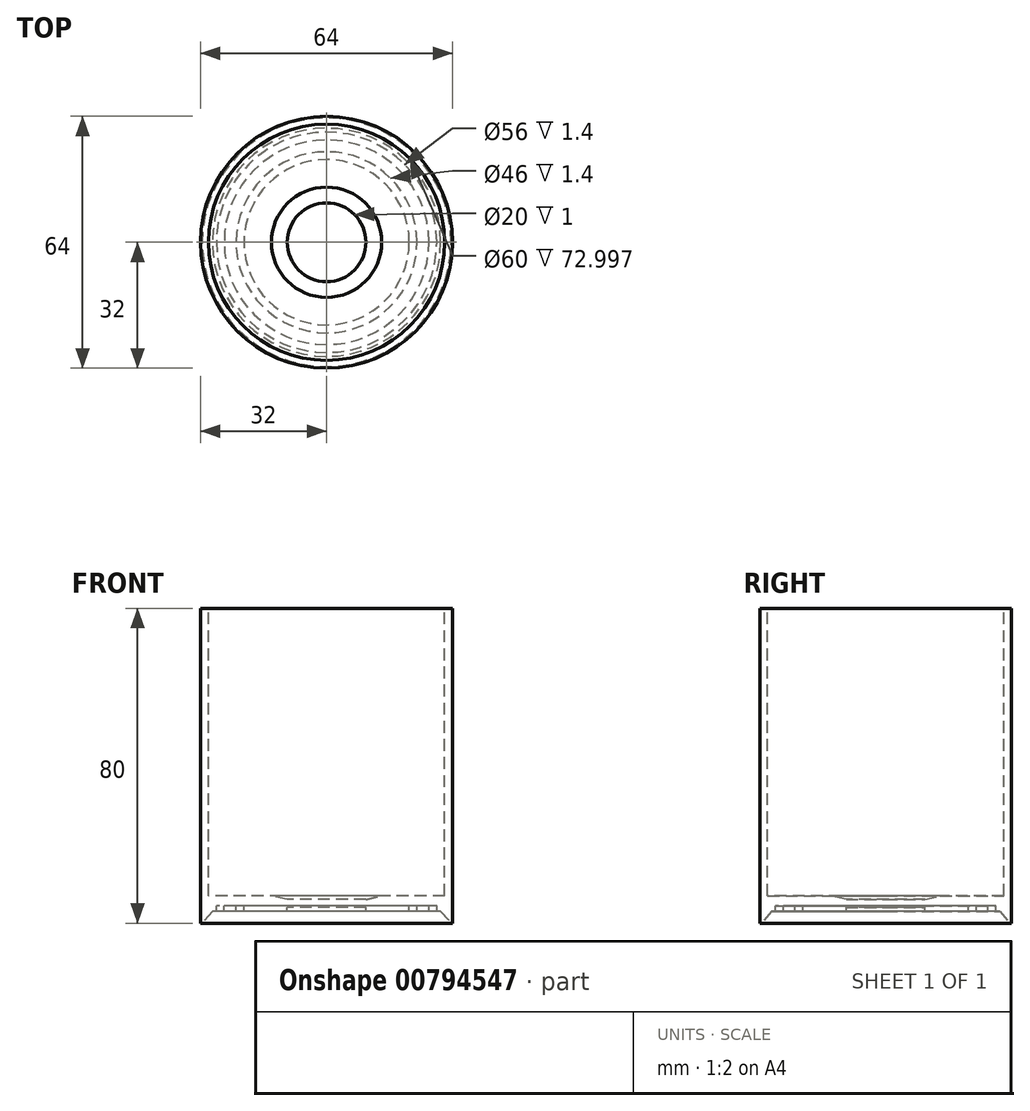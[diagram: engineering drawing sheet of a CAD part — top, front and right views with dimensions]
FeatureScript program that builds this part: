
annotation { "Feature Type Name" : "Feature", "Feature Type Description" : "" }
export const myFeature = defineFeature(function(context is Context, id is Id, definition is map)
    precondition{}
    {
        {
            var Q0;
            Q0=qCreatedBy(makeId("Front.planeOp"),FACE);
            var sketch = newSketch(context, id + "F0", { "sketchPlane" : qUnion([Q0])});
            skLineSegment(sketch, "E0", {"start": v(0, 4) * mm, "end": v(-10, 4) * mm});
            skLineSegment(sketch, "E1", {"start": v(-31.6, 0) * mm, "end": v(-32, 0) * mm});
            skLineSegment(sketch, "E2", {"start": v(-32, 0) * mm, "end": v(-32, 80) * mm});
            skLineSegment(sketch, "E3", {"start": v(-32, 80) * mm, "end": v(-30, 80) * mm});
            skLineSegment(sketch, "E4", {"start": v(-30, 80) * mm, "end": v(-30, 7) * mm});
            skLineSegment(sketch, "E5", {"start": v(-10, 6) * mm, "end": v(0, 6) * mm});
            skLineSegment(sketch, "E6", {"start": v(0, 6) * mm, "end": v(0, 4) * mm});
            skLineSegment(sketch, "E7", {"start": v(-31.6, 0) * mm, "end": v(-29, 3) * mm});
            skLineSegment(sketch, "E8", {"start": v(-29, 3) * mm, "end": v(-28, 3) * mm});
            skLineSegment(sketch, "E9", {"start": v(-10, 3) * mm, "end": v(-10, 4) * mm});
            skLineSegment(sketch, "E10.trimOffspring", {"start": v(-26, 3) * mm, "end": v(-23, 3) * mm});
            skLineSegment(sketch, "E11", {"start": v(-10, 6) * mm, "end": v(-14, 7) * mm});
            skLineSegment(sketch, "E12", {"start": v(-14, 7) * mm, "end": v(-30, 7) * mm});
            skLineSegment(sketch, "E13", {"start": v(-28, 3) * mm, "end": v(-28, 4.4) * mm});
            skLineSegment(sketch, "E14", {"start": v(-28, 4.4) * mm, "end": v(-26, 4.4) * mm});
            skLineSegment(sketch, "E15", {"start": v(-26, 4.4) * mm, "end": v(-26, 3) * mm});
            skLineSegment(sketch, "E16", {"start": v(-23, 3) * mm, "end": v(-23, 4.4) * mm});
            skLineSegment(sketch, "E17", {"start": v(-23, 4.4) * mm, "end": v(-21, 4.4) * mm});
            skLineSegment(sketch, "E18", {"start": v(-21, 4.4) * mm, "end": v(-21, 3) * mm});
            skLineSegment(sketch, "E19.trimOffspring", {"start": v(-21, 3) * mm, "end": v(-10, 3) * mm});
            skSolve(sketch);
        }
        {
            var Q0;
            Q0=makeQuery(id+"F0.imprint","IMPRINT",FACE,{"disambiguationData":[TD([[makeQuery(id+"F0.imprint","IMPRINT",EDGE,{"derivedFrom":sQuery(id+"F0.wireOp",EDGE,"E0")}),-1.0]])]});
            var Q1;
            Q1=sQuery(id+"F0.wireOp",EDGE,"E6");
            revolve(context, id + "F1", {"surfaceOperationType" : NewSurfaceOperationType.NEW, "entities" : qUnion([Q0]), "axis" : qUnion([Q1]), "revolveType" : RevolveType.FULL});
        }
    });
